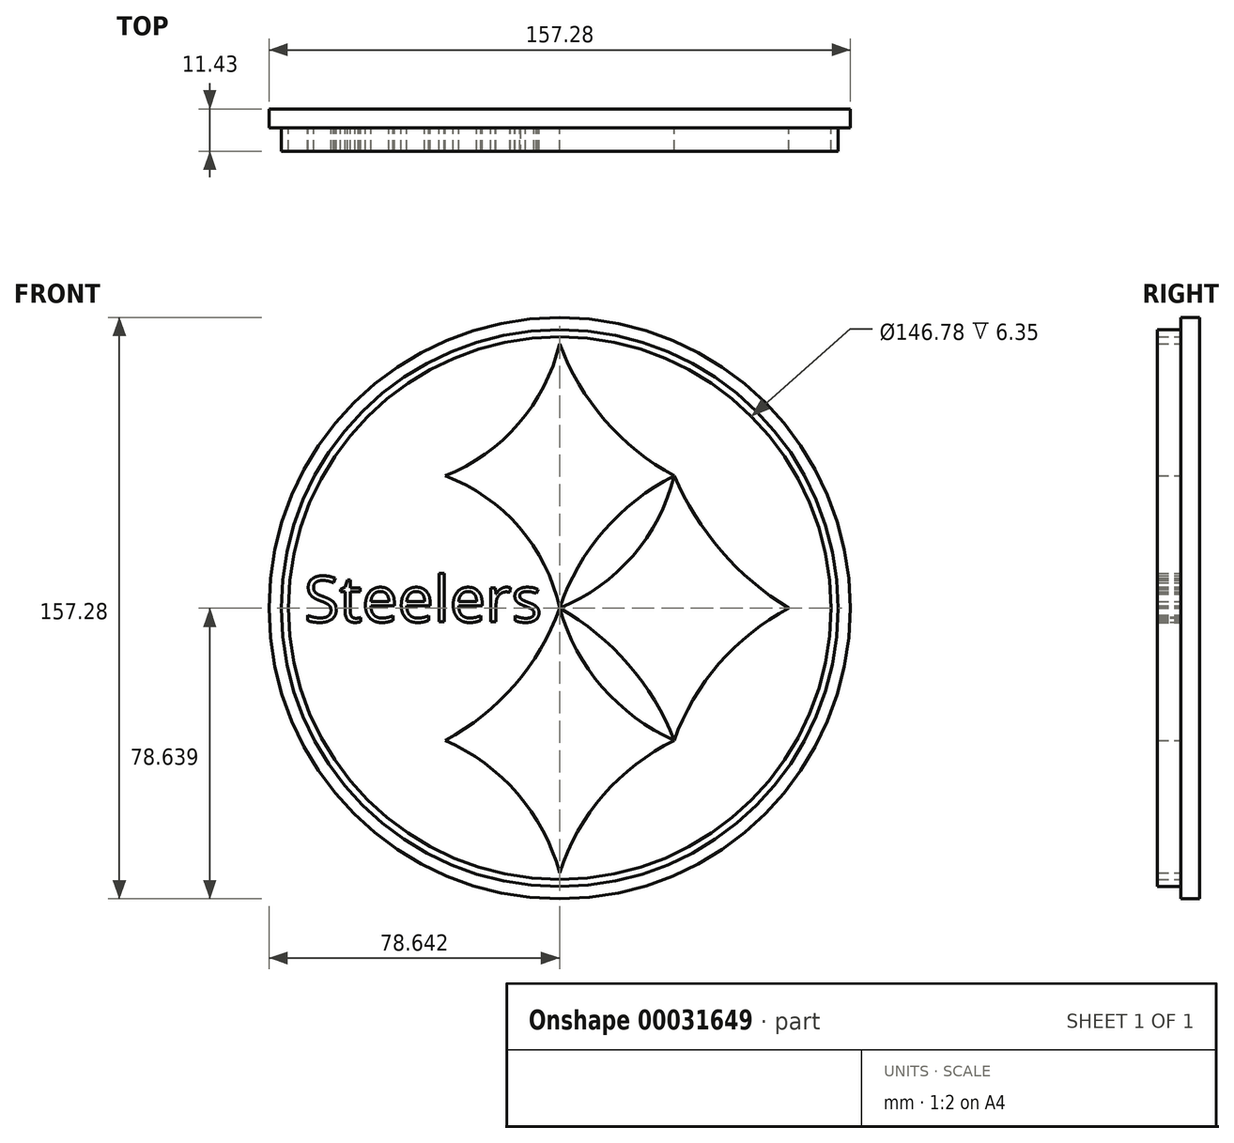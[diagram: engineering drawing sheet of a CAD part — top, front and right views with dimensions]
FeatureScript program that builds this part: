
annotation { "Feature Type Name" : "Feature", "Feature Type Description" : "" }
export const myFeature = defineFeature(function(context is Context, id is Id, definition is map)
    precondition{}
    {
        {
            var Q0;
            Q0=qCreatedBy(makeId("Front.planeOp"),FACE);
            var sketch = newSketch(context, id + "F0", { "sketchPlane" : qUnion([Q0])});
            skCircle(sketch, "E0", {"center": v(-13.79, 6.49) * mm, "radius": 78.64 * mm});
            skSolve(sketch);
        }
        {
            var Q0;
            Q0=makeQuery(id+"F0.imprint","IMPRINT",FACE,{"disambiguationData":[TD([[makeQuery(id+"F0.imprint","IMPRINT",EDGE,{"derivedFrom":sQuery(id+"F0.wireOp",EDGE,"E0")}),1.0]])]});
            extrude(context, id + "F1", {"entities" : qUnion([Q0]), "depth" : 5.08 * mm});
        }
        {
            var Q0;
            Q0=makeQuery(id+"F1.opExtrude","CAP_FACE",FACE,{"disambiguationData":[OSD([sQuery(id+"F0.wireOp",EDGE,"E0")])],"isStart":false});
            var sketch = newSketch(context, id + "F2", { "sketchPlane" : qUnion([Q0])});
            skPoint(sketch, "E1.orphan", {"position": v(-78.93, 36.12) * mm});
            skArc(sketch, "E2", {"start": v(-13.79, 6.49) * mm, "mid": v(-24.67, 28.37) * mm, "end": v(-44.78, 42.27) * mm});
            skArc(sketch, "E3", {"start": v(-44.78, 42.27) * mm, "mid": v(-24.9, 56.36) * mm, "end": v(-13.79, 78.05) * mm});
            skArc(sketch, "E4", {"start": v(-13.79, 78.05) * mm, "mid": v(-1.54, 57.35) * mm, "end": v(17.2, 42.27) * mm});
            skArc(sketch, "E5", {"start": v(17.2, 42.27) * mm, "mid": v(-1.84, 27.45) * mm, "end": v(-13.79, 6.49) * mm});
            skArc(sketch, "E6", {"start": v(17.2, -29.3) * mm, "mid": v(4.8, -8.72) * mm, "end": v(-13.79, 6.49) * mm});
            skArc(sketch, "E7", {"start": v(48.19, 6.49) * mm, "mid": v(29.35, -8.5) * mm, "end": v(17.2, -29.3) * mm});
            skArc(sketch, "E8", {"start": v(17.2, 42.27) * mm, "mid": v(29.93, 21.99) * mm, "end": v(48.19, 6.49) * mm});
            skArc(sketch, "E9", {"start": v(-13.79, 6.49) * mm, "mid": v(6.02, 20.64) * mm, "end": v(17.2, 42.27) * mm});
            skArc(sketch, "E10", {"start": v(-44.78, -29.3) * mm, "mid": v(-25.94, -14.3) * mm, "end": v(-13.79, 6.49) * mm});
            skArc(sketch, "E11", {"start": v(-13.79, 6.49) * mm, "mid": v(-2.27, -14.84) * mm, "end": v(17.2, -29.3) * mm});
            skArc(sketch, "E12", {"start": v(17.2, -29.3) * mm, "mid": v(-1.92, -44.04) * mm, "end": v(-13.79, -65.08) * mm});
            skArc(sketch, "E13", {"start": v(-13.79, -65.08) * mm, "mid": v(-25.22, -43.66) * mm, "end": v(-44.78, -29.3) * mm});
            skPoint(sketch, "E14.orphan", {"position": v(-13.79, 42.27) * mm});
            skPoint(sketch, "E15.end.orphan", {"position": v(-75.77, 42.27) * mm});
            skPoint(sketch, "E16.end.orphan", {"position": v(48.19, 42.27) * mm});
            skPoint(sketch, "E17.orphan", {"position": v(-75.77, -29.3) * mm});
            skPoint(sketch, "E18.start.orphan", {"position": v(-13.79, -29.3) * mm});
            skPoint(sketch, "E19.start.orphan", {"position": v(48.19, -29.3) * mm});
            skSolve(sketch);
        }
        {
            var Q0;
            Q0=makeQuery(id+"F2.imprint","IMPRINT",FACE,{"disambiguationData":[TD([[makeQuery(id+"F2.imprint","IMPRINT",EDGE,{"derivedFrom":sQuery(id+"F2.wireOp",EDGE,"E2")}),-1.0]])]});
            var Q1;
            Q1=makeQuery(id+"F2.imprint","IMPRINT",FACE,{"disambiguationData":[TD([[makeQuery(id+"F2.imprint","IMPRINT",EDGE,{"derivedFrom":sQuery(id+"F2.wireOp",EDGE,"E6")}),-1.0]])]});
            var Q2;
            Q2=makeQuery(id+"F2.imprint","IMPRINT",FACE,{"disambiguationData":[TD([[makeQuery(id+"F2.imprint","IMPRINT",EDGE,{"derivedFrom":sQuery(id+"F2.wireOp",EDGE,"E10")}),-1.0]])]});
            extrude(context, id + "F3", {"entities" : qUnion([Q0, Q1, Q2]), "depth" : 6.35 * mm});
        }
        {
            var Q0;
            Q0=makeQuery(id+"F1.opExtrude","CAP_FACE",FACE,{"disambiguationData":[OSD([sQuery(id+"F0.wireOp",EDGE,"E0")])],"isStart":false});
            var sketch = newSketch(context, id + "F4", { "sketchPlane" : qUnion([Q0])});
            skCircle(sketch, "E20", {"center": v(-13.79, 6.49) * mm, "radius": 73.39 * mm});
            skCircle(sketch, "E21", {"center": v(-13.79, 6.49) * mm, "radius": 75.34 * mm});
            skSolve(sketch);
        }
        {
            var Q0;
            Q0=makeQuery(id+"F4.imprint","IMPRINT",FACE,{"disambiguationData":[TD([[makeQuery(id+"F4.imprint","IMPRINT",EDGE,{"derivedFrom":sQuery(id+"F4.wireOp",EDGE,"E20")}),-1.0]])]});
            extrude(context, id + "F5", {"entities" : qUnion([Q0]), "operationType" : NewBodyOperationType.ADD, "depth" : 6.35 * mm});
        }
        {
            var Q0;
            Q0=makeQuery(id+"F5.boolean.opBoolean","SPLIT",FACE,{"disambiguationData":[TD([makeQuery(id+"F5.opExtrude","SWEPT_FACE",FACE,{"disambiguationData":[OSD([sQuery(id+"F4.wireOp",EDGE,"E20")])]})])],"derivedFrom":makeQuery(id+"F1.opExtrude","CAP_FACE",FACE,{"disambiguationData":[OSD([sQuery(id+"F0.wireOp",EDGE,"E0")])],"isStart":false})});
            var sketch = newSketch(context, id + "F6", { "sketchPlane" : qUnion([Q0])});
            skText(sketch, "E22", { "text": "Steelers", "fontName": "OpenSans-Regular.ttf"});
            const initialGuessF6  = {"E22": [-0.08285, 0.00277, 1, 0, 0.01243]};
            skSetInitialGuess(sketch, initialGuessF6);
            skSolve(sketch);
        }
        {
            var Q0;
            Q0 = qSketchRegion(id + "F6", true);
            extrude(context, id + "F7", {"entities" : qUnion([Q0]), "operationType" : NewBodyOperationType.ADD, "depth" : 6.35 * mm});
        }
    });
